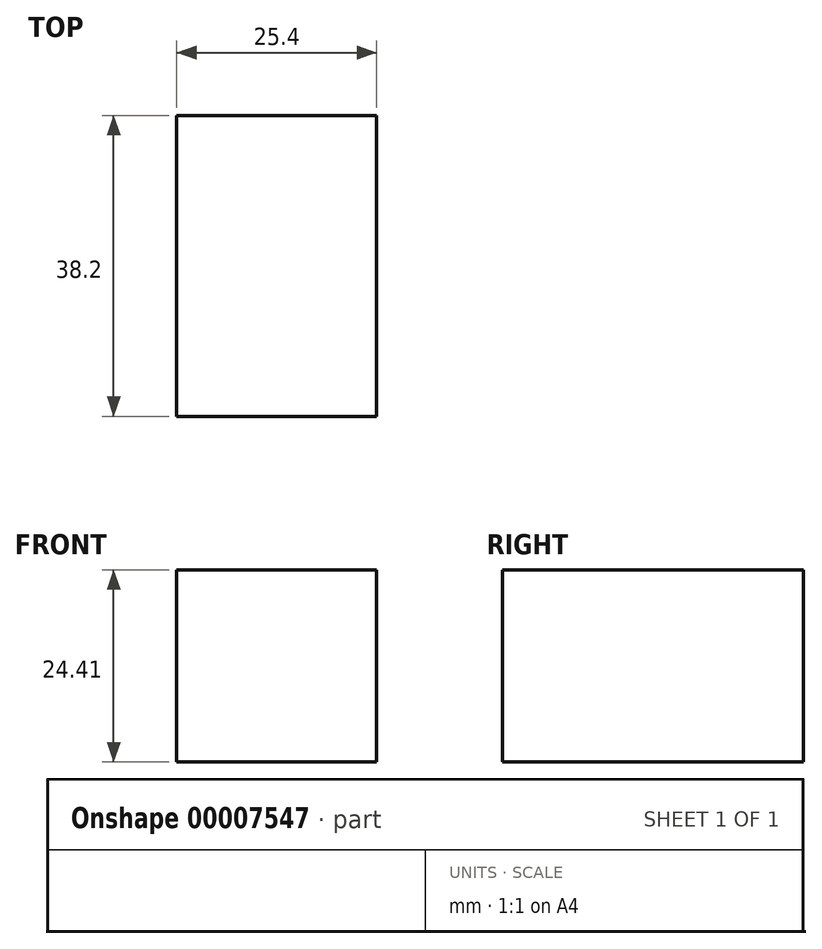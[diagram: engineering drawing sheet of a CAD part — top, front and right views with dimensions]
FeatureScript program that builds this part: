
annotation { "Feature Type Name" : "Feature", "Feature Type Description" : "" }
export const myFeature = defineFeature(function(context is Context, id is Id, definition is map)
    precondition{}
    {
        {
            var Q0;
            Q0=qCreatedBy(makeId("Right.planeOp"),FACE);
            var sketch = newSketch(context, id + "F0", { "sketchPlane" : qUnion([Q0])});
            skLineSegment(sketch, "E0.bottom", {"start": v(0, 0) * mm, "end": v(38.2, 0) * mm});
            skLineSegment(sketch, "E0.top", {"start": v(0, 24.4) * mm, "end": v(38.2, 24.4) * mm});
            skLineSegment(sketch, "E0.left", {"start": v(0, 0) * mm, "end": v(0, 24.4) * mm});
            skLineSegment(sketch, "E0.right", {"start": v(38.2, 0) * mm, "end": v(38.2, 24.4) * mm});
            skSolve(sketch);
        }
        {
            var Q0;
            Q0=makeQuery(id+"F0.imprint","IMPRINT",FACE,{"disambiguationData":[TD([[makeQuery(id+"F0.imprint","IMPRINT",EDGE,{"derivedFrom":sQuery(id+"F0.wireOp",EDGE,"E0.bottom")}),1.0]])]});
            extrude(context, id + "F1", {"entities" : qUnion([Q0]), "depth" : 25.4 * mm});
        }
    });
